# Revit family: VFB_VFB Plus 16-75mm
name_source: partatom
category: Specialty Equipment
revit_build: Autodesk Revit 2015 (Build: 20160512_0715(x64)
units: mm (PartAtom-declared; Revit-internal decimal feet)

## types (60) — shared parameters
Depth = 75 mm
Description = Firefly 102 Ventilated Fire Barrier
IFC Classification = Building Element Proxy
Length = 1000 mm
Manufacturer = Tenmat ltd
Material/Grade = Firefly 102
Performance = BS EN 1366-3:2009 & BS 476, ETA-12/0332, 1224-CPR-0341, CE Marked
URL = https://www.tenmat.com
Youtube Clip = https://www.youtube.com

## per-type parameters (varying)
| type | Seal Type | Tenmat Item Number | Width |
| VFB Plus 16.0 x 75.0 x 1000mm | VFB Plus 60
VFB Plus 60 | I102MP01600075100000
I102MP01600075100000 | 16 mm  [stored 0.0524934 ft] |
| VFB Plus 17.0 x 75.0 x 1000mm | VFB Plus 61 | I102MP01700075100000
I102MP01600075100000 | 17 mm |
| VFB Plus 18.0 x 75.0 x 1000mm | VFB Plus 62 | I102MP01800075100000
I102MP01600075100000 | 18 mm  [stored 0.0590551 ft] |
| VFB Plus 19.0 x 75.0 x 1000mm | VFB Plus 63 | I102MP01900075100000
I102MP01600075100000 | 19 mm  [stored 0.062336 ft] |
| VFB Plus 20.0 x 75.0 x 1000mm | VFB Plus 64 | I102MP02000075100000
I102MP01600075100000 | 20 mm  [stored 0.0656168 ft] |
| VFB Plus 21.0 x 75.0 x 1000mm | VFB Plus 65 | I102MP02100075100000
I102MP01600075100000 | 21 mm  [stored 0.0688976 ft] |
| VFB Plus 22.0 x 75.0 x 1000mm | VFB Plus 66 | I102MP02200075100000
I102MP01600075100000 | 22 mm  [stored 0.0721785 ft] |
| VFB Plus 23.0 x 75.0 x 1000mm | VFB Plus 67 | I102MP02300075100000
I102MP01600075100000 | 23 mm  [stored 0.0754593 ft] |
| VFB Plus 24.0 x 75.0 x 1000mm | VFB Plus 68 | I102MP02400075100000
I102MP01600075100000 | 24 mm  [stored 0.0787402 ft] |
| VFB Plus 25.0 x 75.0 x 1000mm | VFB Plus 69 | I102MP02500075100000
I102MP01600075100000 | 25 mm  [stored 0.082021 ft] |
| VFB Plus 26.0 x 75.0 x 1000mm | VFB Plus 70 | I102MP02600075100000
I102MP01600075100000 | 26 mm |
| VFB Plus 27.0 x 75.0 x 1000mm | VFB Plus 71 | I102MP02700075100000
I102MP01600075100000 | 27 mm  [stored 0.0885827 ft] |
| VFB Plus 28.0 x 75.0 x 1000mm | VFB Plus 72 | I102MP02800075100000
I102MP01600075100000 | 28 mm  [stored 0.0918635 ft] |
| VFB Plus 29.0 x 75.0 x 1000mm | VFB Plus 73 | I102MP02900075100000
I102MP01600075100000 | 29 mm  [stored 0.0951444 ft] |
| VFB Plus 30.0 x 75.0 x 1000mm | VFB Plus 74 | I102MP03000075100000
I102MP01600075100000 | 30 mm  [stored 0.0984252 ft] |
| VFB Plus 31.0 x 75.0 x 1000mm | VFB Plus 75 | I102MP03100075100000
I102MP01600075100000 | 31 mm  [stored 0.101706 ft] |
| VFB Plus 32.0 x 75.0 x 1000mm | VFB Plus 76 | I102MP03200075100000
I102MP01600075100000 | 32 mm  [stored 0.104987 ft] |
| VFB Plus 33.0 x 75.0 x 1000mm | VFB Plus 77 | I102MP03300075100000
I102MP01600075100000 | 33 mm  [stored 0.108268 ft] |
| VFB Plus 34.0 x 75.0 x 1000mm | VFB Plus 78 | I102MP03400075100000
I102MP01600075100000 | 34 mm |
| VFB Plus 35.0 x 75.0 x 1000mm | VFB Plus 79 | I102MP03500075100000
I102MP01600075100000 | 35 mm  [stored 0.114829 ft] |
| VFB Plus 36.0 x 75.0 x 1000mm | VFB Plus 80 | I102MP03600075100000
I102MP01600075100000 | 36 mm  [stored 0.11811 ft] |
| VFB Plus 37.0 x 75.0 x 1000mm | VFB Plus 81 | I102MP03700075100000
I102MP01600075100000 | 37 mm  [stored 0.121391 ft] |
| VFB Plus 38.0 x 75.0 x 1000mm | VFB Plus 82 | I102MP03800075100000
I102MP01600075100000 | 38 mm  [stored 0.124672 ft] |
| VFB Plus 39.0 x 75.0 x 1000mm | VFB Plus 83 | I102MP03900075100000
I102MP01600075100000 | 39 mm  [stored 0.127953 ft] |
| VFB Plus 40.0 x 75.0 x 1000mm | VFB Plus 84 | I102MP04000075100000
I102MP01600075100000 | 40 mm  [stored 0.131234 ft] |
| VFB Plus 41.0 x 75.0 x 1000mm | VFB Plus 85 | I102MP04100075100000
I102MP01600075100000 | 41 mm  [stored 0.134514 ft] |
| VFB Plus 42.0 x 75.0 x 1000mm | VFB Plus 86 | I102MP04200075100000
I102MP01600075100000 | 42 mm  [stored 0.137795 ft] |
| VFB Plus 43.0 x 75.0 x 1000mm | VFB Plus 87 | I102MP04300075100000
I102MP01600075100000 | 43 mm  [stored 0.141076 ft] |
| VFB Plus 44.0 x 75.0 x 1000mm | VFB Plus 88 | I102MP04400075100000
I102MP01600075100000 | 44 mm  [stored 0.144357 ft] |
| VFB Plus 45.0 x 75.0 x 1000mm | VFB Plus 89 | I102MP04500075100000
I102MP01600075100000 | 45 mm  [stored 0.147638 ft] |
| VFB Plus 46.0 x 75.0 x 1000mm | VFB Plus 90 | I102MP04600075100000
I102MP01600075100000 | 46 mm  [stored 0.150919 ft] |
| VFB Plus 47.0 x 75.0 x 1000mm | VFB Plus 91 | I102MP04700075100000
I102MP01600075100000 | 47 mm  [stored 0.154199 ft] |
| VFB Plus 48.0 x 75.0 x 1000mm | VFB Plus 92 | I102MP04800075100000
I102MP01600075100000 | 48 mm  [stored 0.15748 ft] |
| VFB Plus 49.0 x 75.0 x 1000mm | VFB Plus 93 | I102MP04900075100000
I102MP01600075100000 | 49 mm  [stored 0.160761 ft] |
| VFB Plus 50.0 x 75.0 x 1000mm | VFB Plus 94 | I102MP05000075100000
I102MP01600075100000 | 50 mm  [stored 0.164042 ft] |
| VFB Plus 51.0 x 75.0 x 1000mm | VFB Plus 95 | I102MP01600075100000
I102MP05100075100000 | 51 mm |
| VFB Plus 52.0 x 75.0 x 1000mm | VFB Plus 96 | I102MP05200075100000
I102MP01600075100000 | 52 mm |
| VFB Plus 53.0 x 75.0 x 1000mm | VFB Plus 97 | I102MP05300075100000
I102MP01600075100000 | 53 mm  [stored 0.173885 ft] |
| VFB Plus 54.0 x 75.0 x 1000mm | VFB Plus 98 | I102MP05400075100000
I102MP01600075100000 | 54 mm  [stored 0.177165 ft] |
| VFB Plus 55.0 x 75.0 x 1000mm | VFB Plus 99 | I102MP05500075100000
I102MP01600075100000 | 55 mm  [stored 0.180446 ft] |
| VFB Plus 56.0 x 75.0 x 1000mm | VFB Plus 100 | I102MP05600075100000
I102MP01600075100000 | 56 mm |
| VFB Plus 57.0 x 75.0 x 1000mm | VFB Plus 101 | I102MP05700075100000
I102MP01600075100000 | 57 mm |
| VFB Plus 58.0 x 75.0 x 1000mm | VFB Plus 102 | I102MP05800075100000
I102MP01600075100000 | 58 mm |
| VFB Plus 59.0 x 75.0 x 1000mm | VFB Plus 103 | I102MP05900075100000
I102MP01600075100000 | 59 mm |
| VFB Plus 60.0 x 75.0 x 1000mm | VFB Plus 104 | I102MP06000075100000
I102MP01600075100000 | 60 mm |
| VFB Plus 61.0 x 75.0 x 1000mm | VFB Plus 105 | I102MP06100075100000
I102MP01600075100000 | 61 mm |
| VFB Plus 62.0 x 75.0 x 1000mm | VFB Plus 106 | I102MP06200075100000
I102MP01600075100000 | 62 mm |
| VFB Plus 63.0 x 75.0 x 1000mm | VFB Plus 107 | I102MP06300075100000
I102MP01600075100000 | 63 mm |
| VFB Plus 64.0 x 75.0 x 1000mm | VFB Plus 108 | I102MP06400075100000
I102MP01600075100000 | 64 mm |
| VFB Plus 65.0 x 75.0 x 1000mm | VFB Plus 109 | I102MP06500075100000
I102MP01600075100000 | 65 mm |
| VFB Plus 66.0 x 75.0 x 1000mm | VFB Plus 110 | I102MP06600075100000
I102MP01600075100000 | 66 mm |
| VFB Plus 67.0 x 75.0 x 1000mm | VFB Plus 111 | I102MP06700075100000
I102MP01600075100000 | 67 mm |
| VFB Plus 68.0 x 75.0 x 1000mm | VFB Plus 112 | I102MP01600075100000
I102MP06800075100000 | 68 mm |
| VFB Plus 69.0 x 75.0 x 1000mm | VFB Plus 113 | I102MP06900075100000
I102MP01600075100000 | 69 mm |
| VFB Plus 70.0 x 75.0 x 1000mm | VFB Plus 114 | I102MP07000075100000
I102MP01600075100000 | 70 mm |
| VFB Plus 71.0 x 75.0 x 1000mm | VFB Plus 115 | I102MP07100075100000
I102MP01600075100000 | 71 mm |
| VFB Plus 72.0 x 75.0 x 1000mm | VFB Plus 116 | I102MP01600075100000
I102MP07200075100000 | 72 mm |
| VFB Plus 73.0 x 75.0 x 1000mm | VFB Plus 117 | I102MP07300075100000
I102MP01600075100000 | 73 mm |
| VFB Plus 74.0 x 75.0 x 1000mm | VFB Plus 118 | I102MP07400075100000
I102MP01600075100000 | 74 mm |
| VFB Plus 75.0 x 75.0 x 1000mm | VFB Plus 119 | I102MP07500075100000
I102MP01600075100000 | 75 mm |

note: [stored X ft] marks values corroborated as IEEE doubles in the binary element streams (Revit-internal decimal feet)

## geometry (parser evidence)
native form markers: Blend x2, Sweep x3
no freeform markers — native parametric forms only
